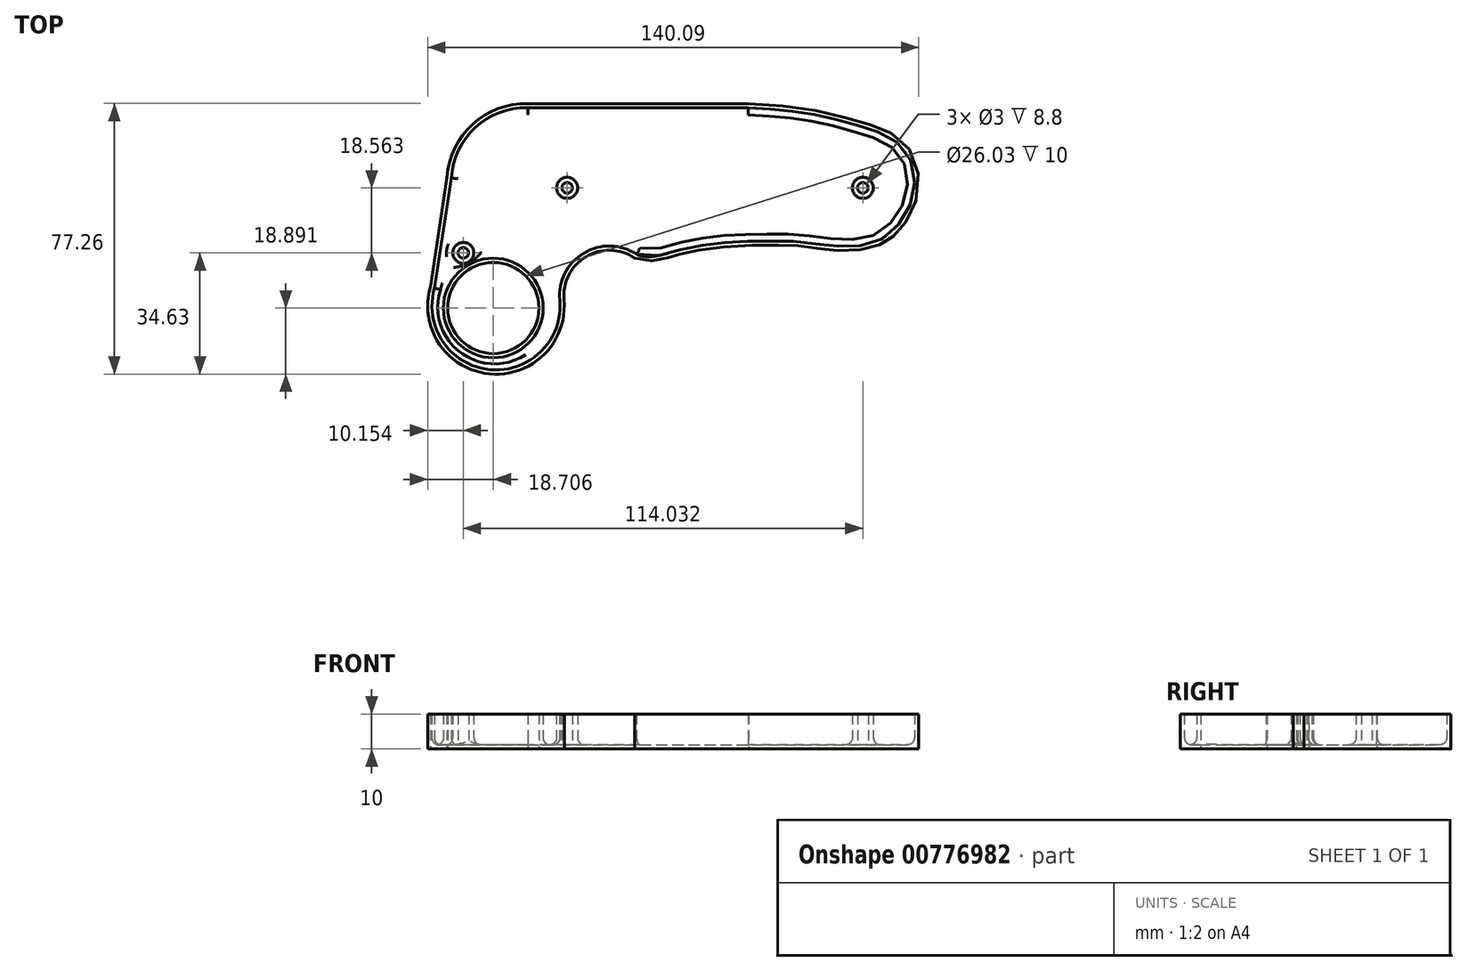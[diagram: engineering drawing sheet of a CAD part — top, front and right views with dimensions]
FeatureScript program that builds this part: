
annotation { "Feature Type Name" : "Feature", "Feature Type Description" : "" }
export const myFeature = defineFeature(function(context is Context, id is Id, definition is map)
    precondition{}
    {
        {
            var Q0;
            Q0=qCreatedBy(makeId("Top.planeOp"),FACE);
            var sketch = newSketch(context, id + "F0", { "sketchPlane" : qUnion([Q0])});
            skCircle(sketch, "E0", {"center": v(-48.32, -13) * mm, "radius": 13.01 * mm});
            skPoint(sketch, "E0.first.point", {"position": v(-47.93, 0) * mm});
            skPoint(sketch, "E0.second.point", {"position": v(-36.23, -17.82) * mm});
            skPoint(sketch, "E0.third.point", {"position": v(-53.28, -25.04) * mm});
            skArc(sketch, "E1", {"start": v(-38.4, 45.35) * mm, "mid": v(-54.21, 39.45) * mm, "end": v(-61.52, 24.24) * mm});
            skPoint(sketch, "E1.first.point", {"position": v(-61.52, 24.24) * mm});
            skPoint(sketch, "E1.second.point", {"position": v(-53.43, 40.13) * mm});
            skPoint(sketch, "E1.third.point", {"position": v(-39.55, 45.35) * mm});
            skArc(sketch, "E2", {"start": v(-66.29, -7.08) * mm, "mid": v(-49.36, -31.82) * mm, "end": v(-28.14, -10.65) * mm});
            skPoint(sketch, "E2.first.point", {"position": v(-28.14, -10.65) * mm});
            skPoint(sketch, "E2.second.point", {"position": v(-49.33, -31.82) * mm});
            skPoint(sketch, "E2.third.point", {"position": v(-66.87, -14.93) * mm});
            skLineSegment(sketch, "E3", {"start": v(-66.29, -7.08) * mm, "end": v(-61.52, 24.24) * mm});
            skArc(sketch, "E4", {"start": v(-8.01, 1.28) * mm, "mid": v(-21.84, 1.67) * mm, "end": v(-28.14, -10.65) * mm});
            skPoint(sketch, "E4.second.point", {"position": v(-25.8, -1.97) * mm});
            skPoint(sketch, "E4.third.point", {"position": v(-11.34, 2.88) * mm});
            skLineSegment(sketch, "E5", {"start": v(-39.55, 45.35) * mm, "end": v(24.5, 45.35) * mm});
            skFitSpline(sketch, "E6", {"points": [v(24.5, 45.35) * mm, v(43.31, 43.47) * mm, v(57.13, 39.94) * mm, v(65.5, 36.72) * mm, v(71.98, 29.4) * mm, v(72.22, 17.33) * mm, v(67.98, 9.7) * mm, v(64.52, 6.49) * mm, v(60.12, 4.36) * mm, v(52.1, 3.34) * mm, v(44.8, 3.97) * mm, v(38.58, 4.76) * mm, v(31.59, 4.91) * mm, v(18.38, 4.52) * mm, v(8.55, 3.18) * mm, v(3.77, 2.1) * mm, v(1.53, 1.37) * mm, v(-3.1, 0.46) * mm, v(-8.01, 1.28) * mm], "startDerivative": vector(232.43, -14.05) * mm, "endDerivative": vector(-108.32, 53.66) * mm});
            skSolve(sketch);
        }
        {
            var Q0;
            Q0 = qSketchRegion(id + "F0", true);
            extrude(context, id + "F1", {"entities" : qUnion([Q0]), "depth" : 10 * mm, "offsetDistance" : 25 * mm});
        }
        {
            var Q0;
            Q0=makeQuery(id+"F1.opExtrude","CAP_FACE",FACE,{"disambiguationData":[OSD([sQuery(id+"F0.wireOp",EDGE,"E0"),sQuery(id+"F0.wireOp",EDGE,"E1"),sQuery(id+"F0.wireOp",EDGE,"E2"),sQuery(id+"F0.wireOp",EDGE,"E3"),sQuery(id+"F0.wireOp",EDGE,"E4"),sQuery(id+"F0.wireOp",EDGE,"E5"),sQuery(id+"F0.wireOp",EDGE,"E6")])],"isStart":false});
            shell(context, id + "F2", {"entities" : qUnion([Q0]), "thickness" : 1.2 * mm});
        }
        {
            var Q0;
            {var subQ0=sQuery(id+"F0.wireOp",EDGE,"E6");var subQ1=sQuery(id+"F0.wireOp",EDGE,"E5");var subQ2=sQuery(id+"F0.wireOp",EDGE,"E4");var subQ3=sQuery(id+"F0.wireOp",EDGE,"E3");var subQ4=sQuery(id+"F0.wireOp",EDGE,"E2");var subQ5=sQuery(id+"F0.wireOp",EDGE,"E1");var subQ6=sQuery(id+"F0.wireOp",EDGE,"E0");Q0=makeQuery(id+"F2.opShell","OFFSET_FACE",FACE,{"disambiguationData":[OSD([subQ6,subQ5,subQ4,subQ3,subQ2,subQ1,subQ0]),TDD([makeQuery(id+"F1.opExtrude","CAP_FACE",FACE,{"disambiguationData":[OSD([subQ6,subQ5,subQ4,subQ3,subQ2,subQ1,subQ0])],"isStart":true})])]});}
            var sketch = newSketch(context, id + "F3", { "sketchPlane" : qUnion([Q0])});
            skCircle(sketch, "E7", {"center": v(-56.88, 2.73) * mm, "radius": 1.5 * mm});
            skCircle(sketch, "E8", {"center": v(-56.88, 2.73) * mm, "radius": 3 * mm});
            skCircle(sketch, "E9", {"center": v(-27.25, 21.3) * mm, "radius": 1.5 * mm});
            skCircle(sketch, "E10", {"center": v(-27.25, 21.3) * mm, "radius": 3 * mm});
            skCircle(sketch, "E11", {"center": v(57.16, 21.3) * mm, "radius": 1.5 * mm});
            skCircle(sketch, "E12", {"center": v(57.16, 21.3) * mm, "radius": 3 * mm});
            skSolve(sketch);
        }
        {
            var Q0;
            Q0 = qSketchRegion(id + "F3", true);
            var Q1;
            Q1=makeQuery(id+"F1.opExtrude","CAP_FACE",FACE,{"disambiguationData":[OSD([sQuery(id+"F0.wireOp",EDGE,"E0"),sQuery(id+"F0.wireOp",EDGE,"E1"),sQuery(id+"F0.wireOp",EDGE,"E2"),sQuery(id+"F0.wireOp",EDGE,"E3"),sQuery(id+"F0.wireOp",EDGE,"E4"),sQuery(id+"F0.wireOp",EDGE,"E5"),sQuery(id+"F0.wireOp",EDGE,"E6")])],"isStart":false});
            extrude(context, id + "F4", {"entities" : qUnion([Q0]), "operationType" : NewBodyOperationType.ADD, "endBound" : BoundingType.UP_TO_SURFACE, "depth" : 25 * mm, "endBoundEntityFace" : qUnion([Q1]), "offsetDistance" : 25 * mm});
        }
        {
            var Q0;
            Q0=makeQuery(id+"F4.opExtrude","CAP_EDGE",EDGE,{"disambiguationData":[OSD([sQuery(id+"F3.wireOp",EDGE,"E10")])],"isStart":true});
            var Q1;
            Q1=makeQuery(id+"F4.opExtrude","CAP_EDGE",EDGE,{"disambiguationData":[OSD([sQuery(id+"F3.wireOp",EDGE,"E12")])],"isStart":true});
            var Q2;
            {var subQ0=sQuery(id+"F0.wireOp",EDGE,"E2");var subQ1=sQuery(id+"F0.wireOp",EDGE,"E1");var subQ2=sQuery(id+"F0.wireOp",EDGE,"E3");var subQ3=sQuery(id+"F0.wireOp",EDGE,"E0");var subQ4=sQuery(id+"F0.wireOp",EDGE,"E4");var subQ5=sQuery(id+"F0.wireOp",EDGE,"E5");var subQ6=sQuery(id+"F0.wireOp",EDGE,"E6");Q2=makeQuery(id+"F4.boolean.opBoolean","SPLIT",FACE,{"disambiguationData":[TD([makeQuery(id+"F2.opShell","OFFSET_FACE",FACE,{"disambiguationData":[OSD([subQ3])]})])],"derivedFrom":makeQuery(id+"F2.opShell","OFFSET_FACE",FACE,{"disambiguationData":[OSD([subQ3,subQ1,subQ0,subQ2,subQ4,subQ5,subQ6]),TDD([makeQuery(id+"F1.opExtrude","CAP_FACE",FACE,{"disambiguationData":[OSD([subQ3,subQ1,subQ0,subQ2,subQ4,subQ5,subQ6])],"isStart":true})])]})});}
            fillet(context, id + "F5", {"entities" : qUnion([Q0, Q1, Q2]), "radius" : 2 * mm, "tangentPropagation" : true, "allowEdgeOverflow" : false});
        }
    });
